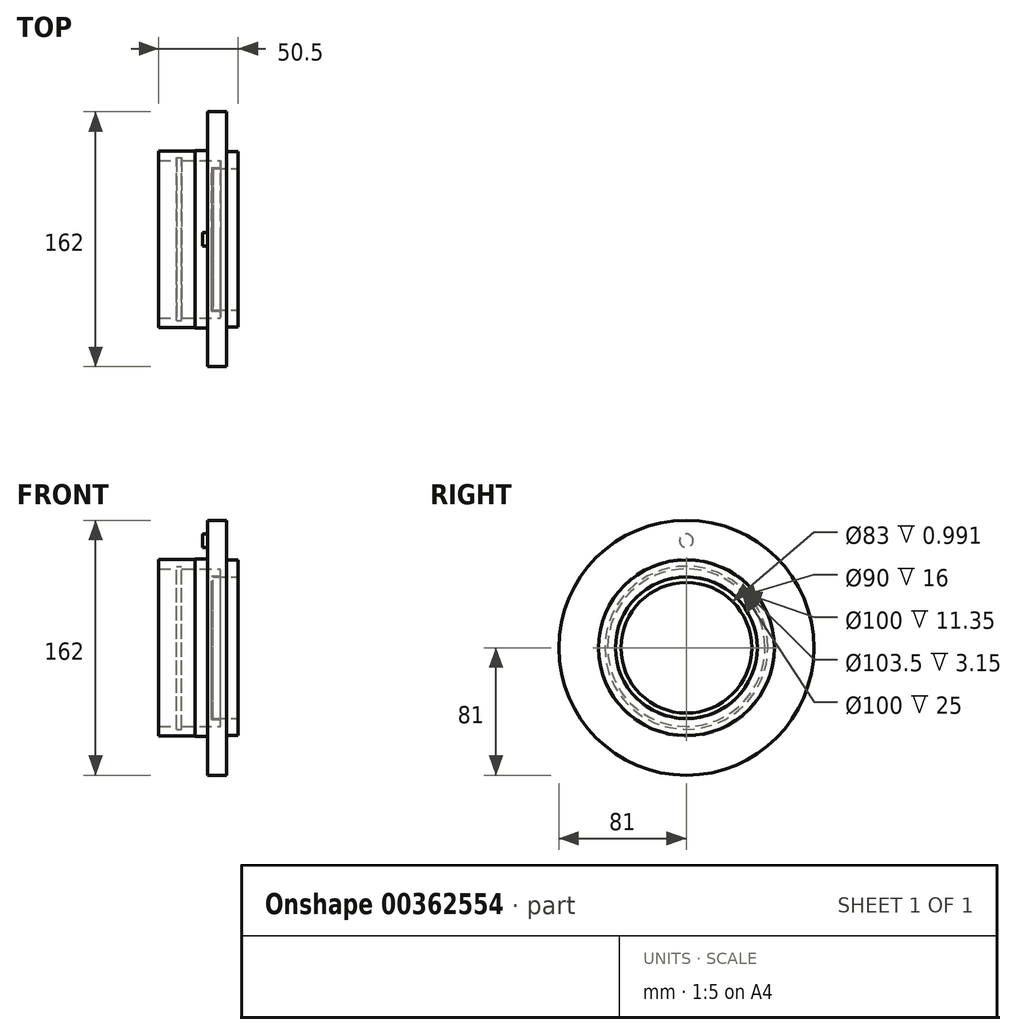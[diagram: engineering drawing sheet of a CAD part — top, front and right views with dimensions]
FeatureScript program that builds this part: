
annotation { "Feature Type Name" : "Feature", "Feature Type Description" : "" }
export const myFeature = defineFeature(function(context is Context, id is Id, definition is map)
    precondition{}
    {
        {
            var Q0;
            Q0=qCreatedBy(makeId("Front.planeOp"),FACE);
            var sketch = newSketch(context, id + "F0", { "sketchPlane" : qUnion([Q0])});
            skLineSegment(sketch, "E0", {"start": v(0, 41.5) * mm, "end": v(0, 45.54) * mm});
            skLineSegment(sketch, "E1", {"start": v(6, 45.54) * mm, "end": v(0, 45.54) * mm});
            skLineSegment(sketch, "E2", {"start": v(6, 45.54) * mm, "end": v(6, 50) * mm});
            skLineSegment(sketch, "E3", {"start": v(6, 50) * mm, "end": v(-19, 50) * mm});
            skLineSegment(sketch, "E4", {"start": v(-19, 50) * mm, "end": v(-19, 51.75) * mm});
            skLineSegment(sketch, "E5", {"start": v(-19, 51.75) * mm, "end": v(-22.16, 51.75) * mm});
            skLineSegment(sketch, "E6", {"start": v(-22.16, 51.75) * mm, "end": v(-22.16, 50) * mm});
            skLineSegment(sketch, "E7", {"start": v(-22.16, 50) * mm, "end": v(-33.5, 50) * mm});
            skLineSegment(sketch, "E8", {"start": v(-33.5, 50) * mm, "end": v(-33.5, 56) * mm});
            skLineSegment(sketch, "E9", {"start": v(-33.5, 56) * mm, "end": v(-10.5, 56) * mm});
            skLineSegment(sketch, "E10", {"start": v(-10.5, 56) * mm, "end": v(-10.5, 56.45) * mm});
            skLineSegment(sketch, "E11", {"start": v(-10.5, 56.45) * mm, "end": v(-2.5, 56.45) * mm});
            skLineSegment(sketch, "E12", {"start": v(-2.5, 56.45) * mm, "end": v(-2.5, 81) * mm});
            skLineSegment(sketch, "E13", {"start": v(-2.5, 81) * mm, "end": v(9.5, 81) * mm});
            skLineSegment(sketch, "E14", {"start": v(9.5, 81) * mm, "end": v(9.5, 55.8) * mm});
            skLineSegment(sketch, "E15", {"start": v(9.5, 55.8) * mm, "end": v(17, 55.8) * mm});
            skLineSegment(sketch, "E16", {"start": v(17, 55.8) * mm, "end": v(17, 45) * mm});
            skLineSegment(sketch, "E17", {"start": v(17, 45) * mm, "end": v(1, 45) * mm});
            skLineSegment(sketch, "E18", {"start": v(1, 45) * mm, "end": v(1, 41.5) * mm});
            skLineSegment(sketch, "E19", {"start": v(1, 41.5) * mm, "end": v(0, 41.5) * mm});
            skLineSegment(sketch, "E20.MirrorCS", {"start": v(-19, -50) * mm, "end": v(-19, -51.75) * mm});
            skLineSegment(sketch, "E21.MirrorCS", {"start": v(-19, -51.75) * mm, "end": v(-22.16, -51.75) * mm});
            skLineSegment(sketch, "E22.MirrorCS", {"start": v(1, -41.5) * mm, "end": v(0, -41.5) * mm});
            skLineSegment(sketch, "E23.MirrorCS", {"start": v(-22.16, -51.75) * mm, "end": v(-22.16, -50) * mm});
            skLineSegment(sketch, "E24.MirrorCS", {"start": v(-10.5, -56) * mm, "end": v(-10.5, -56.45) * mm});
            skLineSegment(sketch, "E25.MirrorCS", {"start": v(6, -45.54) * mm, "end": v(6, -50) * mm});
            skLineSegment(sketch, "E26.MirrorCS", {"start": v(-10.5, -56.45) * mm, "end": v(-2.5, -56.45) * mm});
            skLineSegment(sketch, "E27.MirrorCS", {"start": v(6, -45.54) * mm, "end": v(0, -45.54) * mm});
            skLineSegment(sketch, "E28.MirrorCS", {"start": v(1, -45) * mm, "end": v(1, -41.5) * mm});
            skLineSegment(sketch, "E29.MirrorCS", {"start": v(0, -41.5) * mm, "end": v(0, -45.54) * mm});
            skLineSegment(sketch, "E30.MirrorCS", {"start": v(-22.16, -50) * mm, "end": v(-33.5, -50) * mm});
            skLineSegment(sketch, "E31.MirrorCS", {"start": v(-33.5, -50) * mm, "end": v(-33.5, -56) * mm});
            skLineSegment(sketch, "E32.MirrorCS", {"start": v(-33.5, -56) * mm, "end": v(-10.5, -56) * mm});
            skLineSegment(sketch, "E33.MirrorCS", {"start": v(9.5, -81) * mm, "end": v(9.5, -55.8) * mm});
            skLineSegment(sketch, "E34.MirrorCS", {"start": v(-2.5, -56.45) * mm, "end": v(-2.5, -81) * mm});
            skLineSegment(sketch, "E35.MirrorCS", {"start": v(9.5, -55.8) * mm, "end": v(17, -55.8) * mm});
            skLineSegment(sketch, "E36.MirrorCS", {"start": v(6, -50) * mm, "end": v(-19, -50) * mm});
            skLineSegment(sketch, "E37.MirrorCS", {"start": v(17, -45) * mm, "end": v(1, -45) * mm});
            skLineSegment(sketch, "E38.MirrorCS", {"start": v(-2.5, -81) * mm, "end": v(9.5, -81) * mm});
            skLineSegment(sketch, "E39.MirrorCS", {"start": v(17, -55.8) * mm, "end": v(17, -45) * mm});
            skLineSegment(sketch, "E40", {"start": v(-36.13, 0) * mm, "end": v(52.86, 0) * mm});
            skSolve(sketch);
        }
        {
            var Q0;
            Q0 = qSketchRegion(id + "F0", true);
            var Q1;
            Q1=sQuery(id+"F0.wireOp",EDGE,"E40");
            revolve(context, id + "F1", {"entities" : qUnion([Q0]), "axis" : qUnion([Q1]), "revolveType" : RevolveType.FULL, "oppositeDirection" : true});
        }
        {
            var Q0;
            Q0=makeQuery(id+"F1.opRevolve","SWEPT_FACE",FACE,{"disambiguationData":[OSD([sQuery(id+"F0.wireOp",EDGE,"E14")])]});
            var sketch = newSketch(context, id + "F2", { "sketchPlane" : qUnion([Q0])});
            skCircle(sketch, "E41", {"center": v(0, 68) * mm, "radius": 4.3 * mm});
            skCircle(sketch, "E42", {"center": v(0, 0) * mm, "radius": 68 * mm});
            skSolve(sketch);
        }
        {
            var Q0;
            Q0=makeQuery(id+"F2.imprint","IMPRINT",FACE,{"disambiguationData":[TD([[makeQuery(id+"F2.imprint","IMPRINT",EDGE,{"derivedFrom":sQuery(id+"F2.wireOp",EDGE,"E41")}),1.0]])]});
            extrude(context, id + "F3", {"entities" : qUnion([Q0]), "operationType" : NewBodyOperationType.ADD, "oppositeDirection" : true, "depth" : 15 * mm});
        }
    });
